# Revit family: Bath-Freestanding-Sterling-Performa-71041120
name_source: partatom
category: Plumbing Fixtures
revit_build: Autodesk Revit 2015 (Build: 20140606_1530(x64)
units: mm (PartAtom-declared; Revit-internal decimal feet)

## types (2) — shared parameters
ADA Compliant = Yes
Assembly Code = D2010500
Date Modified = 09/15/2017
Default Elevation = 0"
Description = Performa, Series 7104, 60inch x 29inch Bath - Right-hand Drain
Height = 16 1/4"
Inlet Connection = Inlet Connection
Length = 29 1/4"
Manufacturer = Sterling
MasterFormat 1995 = 15410
MasterFormat 2004 = 22.41.19
Material = Solid Vikrell
Outlet Connection = Outlet Connection
Product Documentation Link = https://www.sterlingplumbing.com
Product Name = Performa
Product Page URL = http://www.sterlingplumbing.com
URL = https://www.sterlingplumbing.com
Waste Connection = Yes
Waste Connection Diameter = 2"
Width = 60"

## per-type parameters (varying)
| type | Finish | Model | Type |
| 60"X29"-0-White | Vikrell- Kohler - 0 - White | 71041120-0 | 1 |
| 60"X29"-96-Biscuit | Vikrell - Kohler - 96 - Biscuit | 71041120-96 | 2 |

## geometry (parser evidence)
native form markers: Blend x8, Sweep x5
no freeform markers — native parametric forms only
